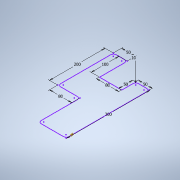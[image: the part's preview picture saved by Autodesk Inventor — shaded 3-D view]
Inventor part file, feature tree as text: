
AUTODESK INVENTOR PART (.ipt)
format: ipt  version: 2021 (Build 250183000, 183)  size: 125,440 bytes
history: native  units: mm
features: other x4, sketch x2, surface_op x2, plane x1, pattern_linear x1
ambient origin geometry x8: Origin, YZ Plane, XZ Plane, XY Plane, X Axis, Y Axis, Z Axis, Center Point
bodies: Body1 (feature_tree), Body2 (feature_tree)
feature tree (10):
  sketch  "Sketch1"  dims[d1=50.0mm]
  plane  "Work Plane1"
  other  "Work Point1"
  pattern_linear  "Rectangular Pattern1"  Count1=30  [1 undecoded]
  sketch  "Sketch2"  dims[d2=50.0mm d3=80.0mm d4=100.0mm d5=50.0mm d6=200.0mm d7=80.0mm d8=10.0mm d9=3.0mm d10=0.0mm d11=20.0mm d13=5.0mm]
  other  "Srf1"
  other  "Work Point2"
  other  "Srf2"
  surface_op  "Boundary Patch1"
  surface_op  "Boundary Patch2"
note: 1 required parameter value undecoded (feature->parameter linkage not recoverable at this tier; creation-order binding heuristic only, values carry confidence <= 0.55)
